FCSTD DOCUMENT  (FreeCAD 0.19R24276 (Git))
Label: Master_sketch
License: All rights reserved
LicenseURL: http://en.wikipedia.org/wiki/All_rights_reserved
objects: Sketcher::SketchObject×1, PartDesign::Body×1
note: 2 computed .brp shape members not serialized (recipe doc carries the construction recipe); baked Part::Feature solids carry a one-line shape summary decoded from their .brp

FEATURE [Sketcher::SketchObject] Sketch
  FullyConstrained = false
  MapMode = 5
  Support = -> [XY_Plane]
  sketch-geometry (4):
    g0: Circle CenterX=-110.946 CenterY=45.7271 CenterZ=0 NormalX=0 NormalY=0 NormalZ=1 AngleXU=0 Radius=8
    g1: Circle CenterX=0 CenterY=0 CenterZ=0 NormalX=0 NormalY=0 NormalZ=1 AngleXU=0 Radius=8
    g2: LineSegment StartX=-110.946 StartY=45.7271 StartZ=0 EndX=0 EndY=0 EndZ=0
    g3: Circle CenterX=-110.946 CenterY=45.7271 CenterZ=0 NormalX=0 NormalY=0 NormalZ=1 AngleXU=0 Radius=22.5
  constraints (8):
    c: Coincident(g1,g-1)
    c: Equal(g0,g1)
    c: Diameter(g1) = 16
    c: Distance(g0,g1) = 120
    c: Coincident(g2,g0)
    c: Coincident(g2,g1)
    c: Coincident(g3,g0)
    c: Diameter(g3) = 45
FEATURE [PartDesign::Body] Body
  Group = -> [Sketch]
  Origin = -> Origin
